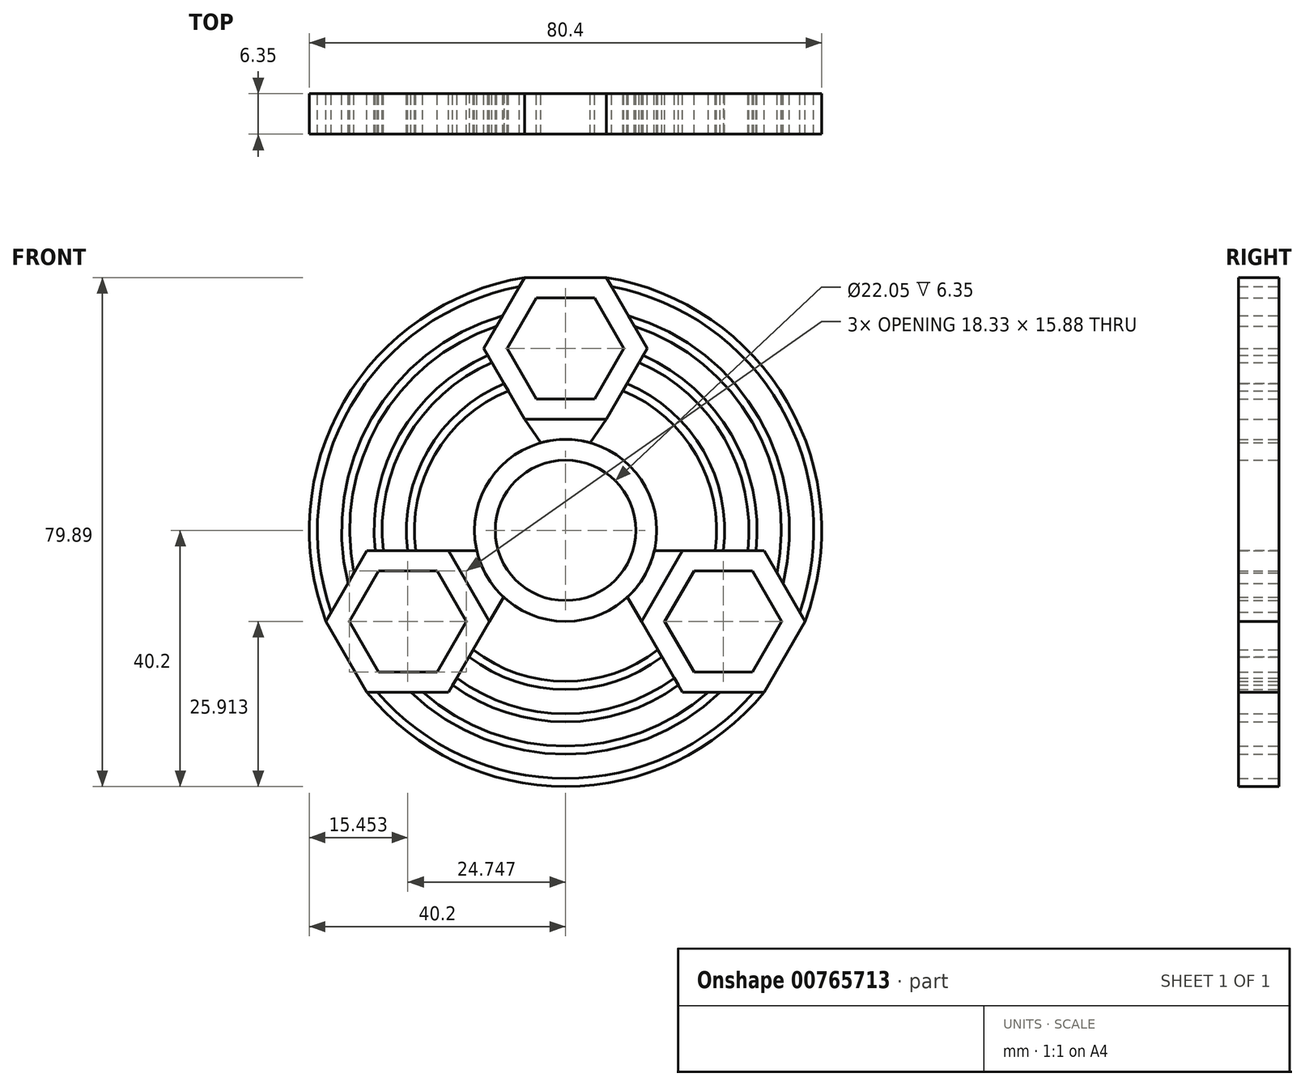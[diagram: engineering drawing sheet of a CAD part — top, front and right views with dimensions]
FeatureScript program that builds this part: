
annotation { "Feature Type Name" : "Feature", "Feature Type Description" : "" }
export const myFeature = defineFeature(function(context is Context, id is Id, definition is map)
    precondition{}
    {
        {
            var Q0;
            Q0=qCreatedBy(makeId("Front.planeOp"),FACE);
            var sketch = newSketch(context, id + "F0", { "sketchPlane" : qUnion([Q0])});
            skCircle(sketch, "E0", {"center": v(0, 0) * mm, "radius": 14.29 * mm});
            skCircle(sketch, "E1", {"center": v(0, 0) * mm, "radius": 11.02 * mm});
            skCircle(sketch, "E2.cCircle", {"center": v(0, 28.58) * mm, "radius": 7.94 * mm, "construction": true});
            skLineSegment(sketch, "E2.0", {"start": v(4.58, 20.64) * mm, "end": v(-4.58, 20.64) * mm});
            skLineSegment(sketch, "E2.1", {"start": v(-4.58, 20.64) * mm, "end": v(-9.17, 28.57) * mm});
            skLineSegment(sketch, "E2.2", {"start": v(-9.17, 28.58) * mm, "end": v(-4.58, 36.51) * mm});
            skLineSegment(sketch, "E2.3", {"start": v(-4.58, 36.51) * mm, "end": v(4.58, 36.51) * mm});
            skLineSegment(sketch, "E2.4", {"start": v(4.58, 36.51) * mm, "end": v(9.17, 28.58) * mm});
            skLineSegment(sketch, "E2.5", {"start": v(9.17, 28.58) * mm, "end": v(4.58, 20.64) * mm});
            skPoint(sketch, "E2.0.midPoint", {"position": v(0, 20.64) * mm});
            skCircle(sketch, "E3.cCircle", {"center": v(0, 28.58) * mm, "radius": 11.11 * mm, "construction": true});
            skLineSegment(sketch, "E3.0", {"start": v(6.42, 17.46) * mm, "end": v(-6.42, 17.46) * mm});
            skLineSegment(sketch, "E3.1", {"start": v(-6.42, 17.46) * mm, "end": v(-12.83, 28.57) * mm});
            skLineSegment(sketch, "E3.2", {"start": v(-12.83, 28.57) * mm, "end": v(-6.42, 39.69) * mm});
            skLineSegment(sketch, "E3.3", {"start": v(-6.42, 39.69) * mm, "end": v(6.42, 39.69) * mm});
            skLineSegment(sketch, "E3.4", {"start": v(6.42, 39.69) * mm, "end": v(12.83, 28.58) * mm});
            skLineSegment(sketch, "E3.5", {"start": v(12.83, 28.58) * mm, "end": v(6.42, 17.46) * mm});
            skPoint(sketch, "E3.0.midPoint", {"position": v(0, 17.46) * mm});
            skPoint(sketch, "E4.1.0", {"position": v(-17.87, -10.32) * mm});
            skLineSegment(sketch, "E4.1.1", {"start": v(-18.33, -25.4) * mm, "end": v(-31.16, -25.4) * mm});
            skLineSegment(sketch, "E4.1.2", {"start": v(-11.92, -14.29) * mm, "end": v(-18.33, -25.4) * mm});
            skLineSegment(sketch, "E4.1.3", {"start": v(-18.33, -3.17) * mm, "end": v(-11.92, -14.29) * mm});
            skCircle(sketch, "E4.1.4", {"center": v(-24.75, -14.29) * mm, "radius": 11.11 * mm, "construction": true});
            skLineSegment(sketch, "E4.1.5", {"start": v(-29.33, -6.35) * mm, "end": v(-20.16, -6.35) * mm});
            skLineSegment(sketch, "E4.1.6", {"start": v(-33.91, -14.29) * mm, "end": v(-29.33, -6.35) * mm});
            skLineSegment(sketch, "E4.1.7", {"start": v(-29.33, -22.22) * mm, "end": v(-33.91, -14.29) * mm});
            skLineSegment(sketch, "E4.1.8", {"start": v(-20.16, -22.22) * mm, "end": v(-29.33, -22.22) * mm});
            skLineSegment(sketch, "E4.1.9", {"start": v(-15.58, -14.29) * mm, "end": v(-20.16, -22.22) * mm});
            skLineSegment(sketch, "E4.1.10", {"start": v(-20.16, -6.35) * mm, "end": v(-15.58, -14.29) * mm});
            skCircle(sketch, "E4.1.11", {"center": v(-24.75, -14.29) * mm, "radius": 7.94 * mm, "construction": true});
            skPoint(sketch, "E4.1.12", {"position": v(-15.12, -8.73) * mm});
            skLineSegment(sketch, "E4.1.13", {"start": v(-31.16, -3.17) * mm, "end": v(-18.33, -3.17) * mm});
            skLineSegment(sketch, "E4.1.14", {"start": v(-37.58, -14.29) * mm, "end": v(-31.16, -3.17) * mm});
            skLineSegment(sketch, "E4.1.15", {"start": v(-31.16, -25.4) * mm, "end": v(-37.58, -14.29) * mm});
            skPoint(sketch, "E4.2.0", {"position": v(17.87, -10.32) * mm});
            skLineSegment(sketch, "E4.2.1", {"start": v(31.16, -3.18) * mm, "end": v(37.58, -14.29) * mm});
            skLineSegment(sketch, "E4.2.2", {"start": v(18.33, -3.18) * mm, "end": v(31.16, -3.18) * mm});
            skLineSegment(sketch, "E4.2.3", {"start": v(11.92, -14.29) * mm, "end": v(18.33, -3.18) * mm});
            skCircle(sketch, "E4.2.4", {"center": v(24.75, -14.29) * mm, "radius": 11.11 * mm, "construction": true});
            skLineSegment(sketch, "E4.2.5", {"start": v(20.16, -22.23) * mm, "end": v(15.58, -14.29) * mm});
            skLineSegment(sketch, "E4.2.6", {"start": v(29.33, -22.23) * mm, "end": v(20.16, -22.23) * mm});
            skLineSegment(sketch, "E4.2.7", {"start": v(33.91, -14.29) * mm, "end": v(29.33, -22.23) * mm});
            skLineSegment(sketch, "E4.2.8", {"start": v(29.33, -6.35) * mm, "end": v(33.91, -14.29) * mm});
            skLineSegment(sketch, "E4.2.9", {"start": v(20.16, -6.35) * mm, "end": v(29.33, -6.35) * mm});
            skLineSegment(sketch, "E4.2.10", {"start": v(15.58, -14.29) * mm, "end": v(20.16, -6.35) * mm});
            skCircle(sketch, "E4.2.11", {"center": v(24.75, -14.29) * mm, "radius": 7.94 * mm, "construction": true});
            skPoint(sketch, "E4.2.12", {"position": v(15.12, -8.73) * mm});
            skLineSegment(sketch, "E4.2.13", {"start": v(18.33, -25.4) * mm, "end": v(11.92, -14.29) * mm});
            skLineSegment(sketch, "E4.2.14", {"start": v(31.16, -25.4) * mm, "end": v(18.33, -25.4) * mm});
            skLineSegment(sketch, "E4.2.15", {"start": v(37.58, -14.29) * mm, "end": v(31.16, -25.4) * mm});
            skSolve(sketch);
        }
        {
            var Q0;
            Q0=qCreatedBy(makeId("Front.planeOp"),FACE);
            var sketch = newSketch(context, id + "F1", { "sketchPlane" : qUnion([Q0])});
            skLineSegment(sketch, "E5.0", {"start": v(6.42, 17.46) * mm, "end": v(-6.42, 17.46) * mm});
            skLineSegment(sketch, "E5.1", {"start": v(-12.83, 28.57) * mm, "end": v(-6.42, 39.69) * mm});
            skCircle(sketch, "E5.2", {"center": v(0, 28.58) * mm, "radius": 11.11 * mm});
            skLineSegment(sketch, "E5.3", {"start": v(-11.92, -14.29) * mm, "end": v(-18.33, -25.4) * mm});
            skLineSegment(sketch, "E5.4", {"start": v(11.92, -14.29) * mm, "end": v(18.33, -3.18) * mm});
            skLineSegment(sketch, "E5.5", {"start": v(29.33, -6.35) * mm, "end": v(33.91, -14.29) * mm});
            skLineSegment(sketch, "E5.6", {"start": v(-33.91, -14.29) * mm, "end": v(-29.33, -6.35) * mm});
            skLineSegment(sketch, "E5.7", {"start": v(-6.42, 17.46) * mm, "end": v(-12.83, 28.57) * mm});
            skLineSegment(sketch, "E5.8", {"start": v(-15.58, -14.29) * mm, "end": v(-20.16, -22.22) * mm});
            skLineSegment(sketch, "E5.9", {"start": v(9.17, 28.58) * mm, "end": v(4.58, 20.64) * mm});
            skCircle(sketch, "E5.10", {"center": v(24.75, -14.29) * mm, "radius": 7.94 * mm});
            skLineSegment(sketch, "E5.11", {"start": v(-37.58, -14.29) * mm, "end": v(-31.16, -3.17) * mm});
            skLineSegment(sketch, "E5.12", {"start": v(-18.33, -25.4) * mm, "end": v(-31.16, -25.4) * mm});
            skLineSegment(sketch, "E5.13", {"start": v(-31.16, -25.4) * mm, "end": v(-37.58, -14.29) * mm});
            skLineSegment(sketch, "E5.14", {"start": v(33.91, -14.29) * mm, "end": v(29.33, -22.23) * mm});
            skLineSegment(sketch, "E5.15", {"start": v(31.16, -25.4) * mm, "end": v(18.33, -25.4) * mm});
            skCircle(sketch, "E5.16", {"center": v(-24.75, -14.29) * mm, "radius": 7.94 * mm});
            skCircle(sketch, "E5.17", {"center": v(-24.75, -14.29) * mm, "radius": 11.11 * mm});
            skLineSegment(sketch, "E5.18", {"start": v(29.33, -22.23) * mm, "end": v(20.16, -22.23) * mm});
            skLineSegment(sketch, "E5.19", {"start": v(-29.33, -6.35) * mm, "end": v(-20.16, -6.35) * mm});
            skLineSegment(sketch, "E5.20", {"start": v(-6.42, 39.69) * mm, "end": v(6.42, 39.69) * mm});
            skLineSegment(sketch, "E5.21", {"start": v(6.42, 39.69) * mm, "end": v(12.83, 28.58) * mm});
            skLineSegment(sketch, "E5.22", {"start": v(12.83, 28.58) * mm, "end": v(6.42, 17.46) * mm});
            skCircle(sketch, "E5.23", {"center": v(0, 0) * mm, "radius": 14.29 * mm});
            skCircle(sketch, "E5.24", {"center": v(0, 0) * mm, "radius": 11.02 * mm});
            skLineSegment(sketch, "E5.25", {"start": v(-20.16, -22.22) * mm, "end": v(-29.33, -22.22) * mm});
            skCircle(sketch, "E5.26", {"center": v(0, 28.58) * mm, "radius": 7.94 * mm});
            skLineSegment(sketch, "E5.27", {"start": v(-31.16, -3.17) * mm, "end": v(-18.33, -3.17) * mm});
            skLineSegment(sketch, "E5.28", {"start": v(-4.58, 20.64) * mm, "end": v(-9.17, 28.57) * mm});
            skLineSegment(sketch, "E5.29", {"start": v(-9.17, 28.58) * mm, "end": v(-4.58, 36.51) * mm});
            skLineSegment(sketch, "E5.30", {"start": v(-4.58, 36.51) * mm, "end": v(4.58, 36.51) * mm});
            skLineSegment(sketch, "E5.31", {"start": v(4.58, 36.51) * mm, "end": v(9.17, 28.58) * mm});
            skCircle(sketch, "E5.32", {"center": v(24.75, -14.29) * mm, "radius": 11.11 * mm});
            skLineSegment(sketch, "E5.33", {"start": v(18.33, -25.4) * mm, "end": v(11.92, -14.29) * mm});
            skLineSegment(sketch, "E5.34", {"start": v(-29.33, -22.22) * mm, "end": v(-33.91, -14.29) * mm});
            skLineSegment(sketch, "E5.35", {"start": v(18.33, -3.18) * mm, "end": v(31.16, -3.18) * mm});
            skLineSegment(sketch, "E5.36", {"start": v(20.16, -6.35) * mm, "end": v(29.33, -6.35) * mm});
            skLineSegment(sketch, "E5.37", {"start": v(-18.33, -3.17) * mm, "end": v(-11.92, -14.29) * mm});
            skLineSegment(sketch, "E5.38", {"start": v(20.16, -22.23) * mm, "end": v(15.58, -14.29) * mm});
            skLineSegment(sketch, "E6.0", {"start": v(31.16, -3.18) * mm, "end": v(37.58, -14.29) * mm});
            skLineSegment(sketch, "E6.25", {"start": v(15.58, -14.29) * mm, "end": v(20.16, -6.35) * mm});
            skLineSegment(sketch, "E6.27", {"start": v(4.58, 20.64) * mm, "end": v(-4.58, 20.64) * mm});
            skLineSegment(sketch, "E6.34", {"start": v(-20.16, -6.35) * mm, "end": v(-15.58, -14.29) * mm});
            skArc(sketch, "E7", {"start": v(-31.16, -25.4) * mm, "mid": v(0, -40.2) * mm, "end": v(31.16, -25.4) * mm});
            skArc(sketch, "E8", {"start": v(-7.24, 38.26) * mm, "mid": v(-33.72, 19.47) * mm, "end": v(-36.75, -12.86) * mm});
            skArc(sketch, "E9.trimOffspring", {"start": v(-29.51, -25.4) * mm, "mid": v(0, -38.94) * mm, "end": v(29.51, -25.4) * mm});
            skArc(sketch, "E10.trimOffspring", {"start": v(-6.42, 39.69) * mm, "mid": v(-34.82, 20.1) * mm, "end": v(-37.58, -14.29) * mm});
            skArc(sketch, "E11.trimOffspring", {"start": v(36.75, -12.86) * mm, "mid": v(33.72, 19.47) * mm, "end": v(7.24, 38.26) * mm});
            skArc(sketch, "E12.trimOffspring", {"start": v(37.58, -14.29) * mm, "mid": v(34.82, 20.1) * mm, "end": v(6.42, 39.69) * mm});
            skLineSegment(sketch, "E13", {"start": v(31.16, -25.4) * mm, "end": v(37.58, -14.29) * mm});
            skArc(sketch, "E14", {"start": v(-6.42, 33.24) * mm, "mid": v(-6.45, 33.24) * mm, "end": v(-6.48, 33.23) * mm});
            skArc(sketch, "E15.trimOffspring", {"start": v(6.48, 33.23) * mm, "mid": v(6.45, 33.24) * mm, "end": v(6.42, 33.24) * mm});
            skArc(sketch, "E16.trimOffspring", {"start": v(-9.86, 33.71) * mm, "mid": v(-30.42, 17.56) * mm, "end": v(-34.13, -8.31) * mm});
            skArc(sketch, "E17.trimOffspring", {"start": v(-10.8, 32.09) * mm, "mid": v(-29.32, 16.93) * mm, "end": v(-33.2, -6.69) * mm});
            skArc(sketch, "E18.trimOffspring", {"start": v(-32.02, -11) * mm, "mid": v(-32, -11.04) * mm, "end": v(-32, -11.06) * mm});
            skArc(sketch, "E19.trimOffspring", {"start": v(-25.58, -22.18) * mm, "mid": v(-25.56, -22.2) * mm, "end": v(-25.54, -22.22) * mm});
            skArc(sketch, "E20.trimOffspring", {"start": v(-22.39, -25.4) * mm, "mid": v(0, -33.86) * mm, "end": v(22.39, -25.4) * mm});
            skArc(sketch, "E21.trimOffspring", {"start": v(-24.27, -25.4) * mm, "mid": v(0, -35.13) * mm, "end": v(24.27, -25.4) * mm});
            skArc(sketch, "E22.trimOffspring", {"start": v(25.54, -22.23) * mm, "mid": v(25.56, -22.2) * mm, "end": v(25.58, -22.18) * mm});
            skArc(sketch, "E23.trimOffspring", {"start": v(32, -11.06) * mm, "mid": v(32, -11.04) * mm, "end": v(32.02, -11) * mm});
            skArc(sketch, "E24.trimOffspring", {"start": v(33.2, -6.69) * mm, "mid": v(29.32, 16.93) * mm, "end": v(10.8, 32.09) * mm});
            skArc(sketch, "E25.trimOffspring", {"start": v(34.13, -8.31) * mm, "mid": v(30.42, 17.56) * mm, "end": v(9.86, 33.71) * mm});
            skArc(sketch, "E26.trimOffspring", {"start": v(-12.2, 27.46) * mm, "mid": v(-26.02, 15.02) * mm, "end": v(-29.88, -3.17) * mm});
            skArc(sketch, "E27.trimOffspring", {"start": v(-11.55, 26.36) * mm, "mid": v(-24.92, 14.39) * mm, "end": v(-28.6, -3.17) * mm});
            skArc(sketch, "E28.trimOffspring", {"start": v(-17.69, -24.29) * mm, "mid": v(0, -30.05) * mm, "end": v(17.69, -24.29) * mm});
            skArc(sketch, "E29.trimOffspring", {"start": v(-17.05, -23.18) * mm, "mid": v(0, -28.78) * mm, "end": v(17.05, -23.18) * mm});
            skArc(sketch, "E30.trimOffspring", {"start": v(29.88, -3.18) * mm, "mid": v(26.02, 15.02) * mm, "end": v(12.2, 27.46) * mm});
            skArc(sketch, "E31.trimOffspring", {"start": v(28.6, -3.18) * mm, "mid": v(24.92, 14.39) * mm, "end": v(11.55, 26.36) * mm});
            skLineSegment(sketch, "E32", {"start": v(-18.33, -3.17) * mm, "end": v(-13.93, -3.17) * mm});
            skLineSegment(sketch, "E33", {"start": v(-11.92, -14.29) * mm, "end": v(-9.71, -10.48) * mm});
            skLineSegment(sketch, "E34", {"start": v(11.92, -14.29) * mm, "end": v(9.71, -10.48) * mm});
            skLineSegment(sketch, "E35", {"start": v(18.33, -3.18) * mm, "end": v(13.93, -3.18) * mm});
            skLineSegment(sketch, "E36", {"start": v(6.42, 17.46) * mm, "end": v(3.9, 13.75) * mm});
            skLineSegment(sketch, "E37", {"start": v(-6.42, 17.46) * mm, "end": v(-3.9, 13.75) * mm});
            skArc(sketch, "E38", {"start": v(-9.63, 23.04) * mm, "mid": v(-21.62, 12.48) * mm, "end": v(-24.77, -3.17) * mm});
            skArc(sketch, "E39", {"start": v(-9, 21.93) * mm, "mid": v(-20.52, 11.85) * mm, "end": v(-23.48, -3.18) * mm});
            skArc(sketch, "E40.trimOffspring", {"start": v(23.47, -3.25) * mm, "mid": v(20.54, 11.82) * mm, "end": v(9, 21.93) * mm});
            skArc(sketch, "E41.trimOffspring", {"start": v(24.77, -3.18) * mm, "mid": v(21.62, 12.48) * mm, "end": v(9.63, 23.04) * mm});
            skArc(sketch, "E42.trimOffspring", {"start": v(-15.13, -19.86) * mm, "mid": v(0, -24.97) * mm, "end": v(15.13, -19.86) * mm});
            skArc(sketch, "E43.trimOffspring", {"start": v(-14.5, -18.75) * mm, "mid": v(0, -23.7) * mm, "end": v(14.5, -18.75) * mm});
            skSolve(sketch);
        }
        {
            var Q0;
            Q0 = qSketchRegion(id + "F0", true);
            var Q1;
            {var subQ2=sQuery(id+"F1.wireOp",EDGE,"E8");Q1=makeQuery(id+"F1.imprint","IMPRINT",FACE,{"disambiguationData":[TD([[makeQuery(id+"F1.imprint","IMPRINT",EDGE,{"derivedFrom":subQ2}),-1.0]])]});}
            var Q2;
            {var subQ0=sQuery(id+"F1.wireOp",EDGE,"E16.trimOffspring");Q2=makeQuery(id+"F1.imprint","IMPRINT",FACE,{"disambiguationData":[TD([[makeQuery(id+"F1.imprint","IMPRINT",EDGE,{"derivedFrom":subQ0}),1.0]])]});}
            var Q3;
            {var subQ4=sQuery(id+"F1.wireOp",EDGE,"E38");Q3=makeQuery(id+"F1.imprint","IMPRINT",FACE,{"disambiguationData":[TD([[makeQuery(id+"F1.imprint","IMPRINT",EDGE,{"derivedFrom":subQ4}),1.0]])]});}
            var Q4;
            {var subQ0=sQuery(id+"F1.wireOp",EDGE,"E26.trimOffspring");Q4=makeQuery(id+"F1.imprint","IMPRINT",FACE,{"disambiguationData":[TD([[makeQuery(id+"F1.imprint","IMPRINT",EDGE,{"derivedFrom":subQ0}),1.0]])]});}
            var Q5;
            {var subQ7=sQuery(id+"F1.wireOp",EDGE,"E42.trimOffspring");Q5=makeQuery(id+"F1.imprint","IMPRINT",FACE,{"disambiguationData":[TD([[makeQuery(id+"F1.imprint","IMPRINT",EDGE,{"derivedFrom":subQ7}),1.0]])]});}
            var Q6;
            {var subQ0=sQuery(id+"F1.wireOp",EDGE,"E28.trimOffspring");Q6=makeQuery(id+"F1.imprint","IMPRINT",FACE,{"disambiguationData":[TD([[makeQuery(id+"F1.imprint","IMPRINT",EDGE,{"derivedFrom":subQ0}),1.0]])]});}
            var Q7;
            {var subQ0=sQuery(id+"F1.wireOp",EDGE,"E7");Q7=makeQuery(id+"F1.imprint","IMPRINT",FACE,{"disambiguationData":[TD([[makeQuery(id+"F1.imprint","IMPRINT",EDGE,{"derivedFrom":subQ0}),1.0]])]});}
            var Q8;
            {var subQ0=sQuery(id+"F1.wireOp",EDGE,"E20.trimOffspring");Q8=makeQuery(id+"F1.imprint","IMPRINT",FACE,{"disambiguationData":[TD([[makeQuery(id+"F1.imprint","IMPRINT",EDGE,{"derivedFrom":subQ0}),-1.0]])]});}
            var Q9;
            {var subQ5=sQuery(id+"F1.wireOp",EDGE,"E41.trimOffspring");Q9=makeQuery(id+"F1.imprint","IMPRINT",FACE,{"disambiguationData":[TD([[makeQuery(id+"F1.imprint","IMPRINT",EDGE,{"derivedFrom":subQ5}),1.0]])]});}
            var Q10;
            {var subQ0=sQuery(id+"F1.wireOp",EDGE,"E30.trimOffspring");Q10=makeQuery(id+"F1.imprint","IMPRINT",FACE,{"disambiguationData":[TD([[makeQuery(id+"F1.imprint","IMPRINT",EDGE,{"derivedFrom":subQ0}),1.0]])]});}
            var Q11;
            {var subQ0=sQuery(id+"F1.wireOp",EDGE,"E24.trimOffspring");Q11=makeQuery(id+"F1.imprint","IMPRINT",FACE,{"disambiguationData":[TD([[makeQuery(id+"F1.imprint","IMPRINT",EDGE,{"derivedFrom":subQ0}),-1.0]])]});}
            var Q12;
            {var subQ2=sQuery(id+"F1.wireOp",EDGE,"E11.trimOffspring");Q12=makeQuery(id+"F1.imprint","IMPRINT",FACE,{"disambiguationData":[TD([[makeQuery(id+"F1.imprint","IMPRINT",EDGE,{"derivedFrom":subQ2}),-1.0]])]});}
            var Q13;
            {var subQ0=sQuery(id+"F1.wireOp",EDGE,"E34");Q13=makeQuery(id+"F1.imprint","IMPRINT",FACE,{"disambiguationData":[TD([[makeQuery(id+"F1.imprint","IMPRINT",EDGE,{"derivedFrom":subQ0}),-1.0]])]});}
            var Q14;
            {var subQ0=sQuery(id+"F1.wireOp",EDGE,"E36");Q14=makeQuery(id+"F1.imprint","IMPRINT",FACE,{"disambiguationData":[TD([[makeQuery(id+"F1.imprint","IMPRINT",EDGE,{"derivedFrom":subQ0}),-1.0]])]});}
            var Q15;
            {var subQ0=sQuery(id+"F1.wireOp",EDGE,"E32");Q15=makeQuery(id+"F1.imprint","IMPRINT",FACE,{"disambiguationData":[TD([[makeQuery(id+"F1.imprint","IMPRINT",EDGE,{"derivedFrom":subQ0}),-1.0]])]});}
            extrude(context, id + "F2", {"entities" : qUnion([Q0, Q1, Q2, Q3, Q4, Q5, Q6, Q7, Q8, Q9, Q10, Q11, Q12, Q13, Q14, Q15]), "depth" : 6.35 * mm, "offsetDistance" : 25.4 * mm});
        }
    });
